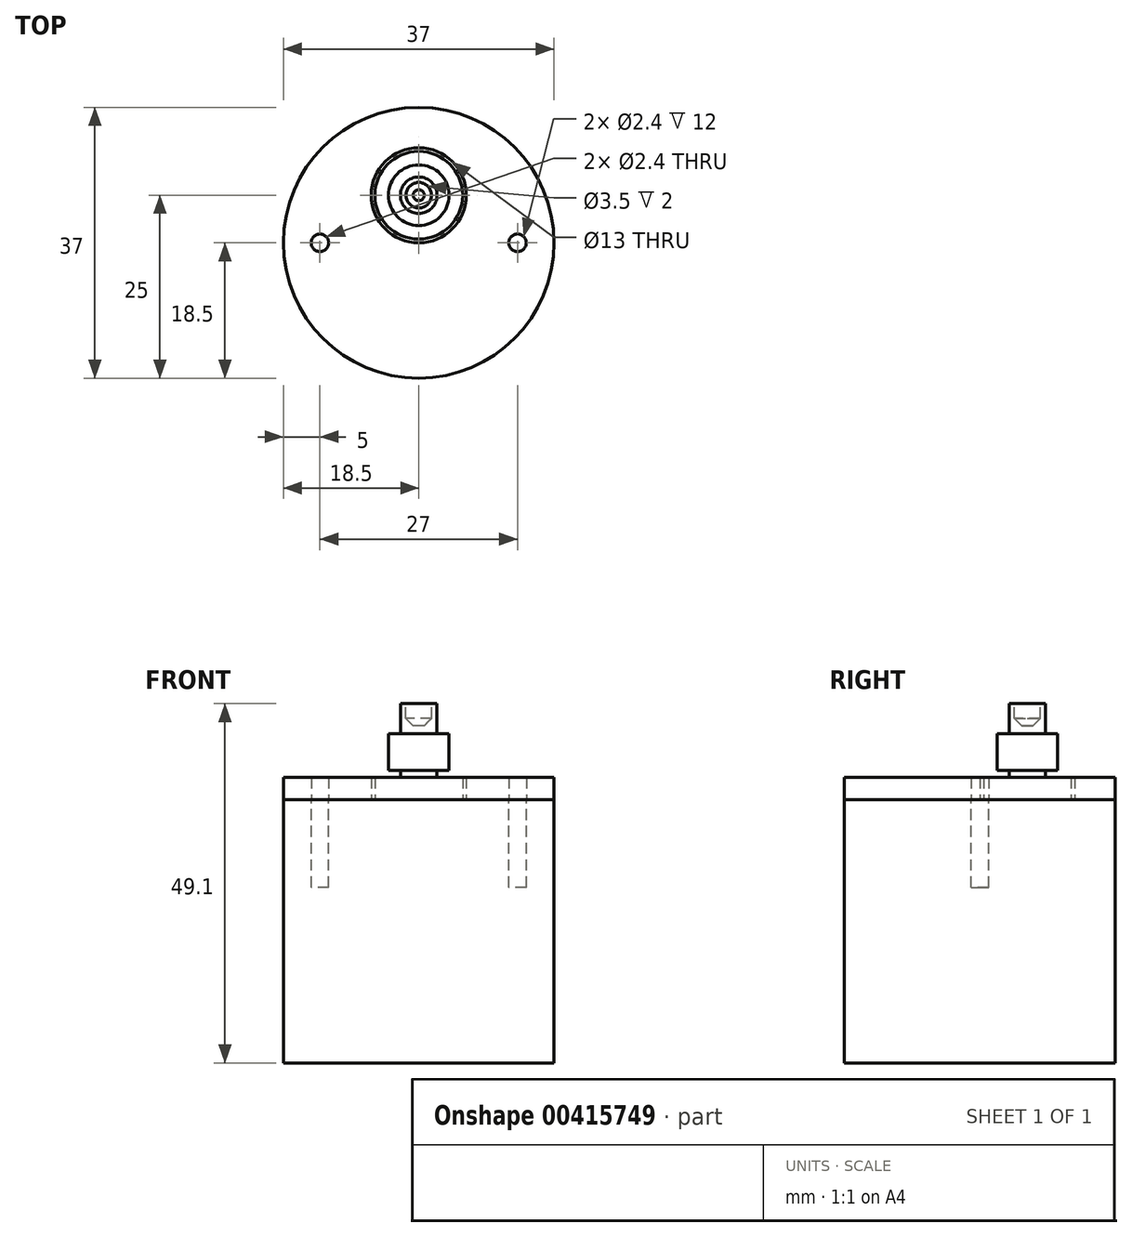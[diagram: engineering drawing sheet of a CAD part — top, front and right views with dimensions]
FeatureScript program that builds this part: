
annotation { "Feature Type Name" : "Feature", "Feature Type Description" : "" }
export const myFeature = defineFeature(function(context is Context, id is Id, definition is map)
    precondition{}
    {
        {
            var Q0;
            Q0=qCreatedBy(makeId("Top.planeOp"),FACE);
            var sketch = newSketch(context, id + "F0", { "sketchPlane" : qUnion([Q0])});
            skCircle(sketch, "E0", {"center": v(0, 0) * mm, "radius": 18.5 * mm});
            skSolve(sketch);
        }
        {
            var Q0;
            Q0=makeQuery(id+"F0.imprint","IMPRINT",FACE,{"disambiguationData":[TD([[makeQuery(id+"F0.imprint","IMPRINT",EDGE,{"derivedFrom":sQuery(id+"F0.wireOp",EDGE,"E0")}),1.0]])]});
            var Q1;
            Q1=sQuery(id+"F0.wireOp",EDGE,"E0");
            extrude(context, id + "F1", {"entities" : qUnion([Q0]), "surfaceEntities" : qUnion([Q1]), "oppositeDirection" : true, "depth" : 36 * mm});
        }
        {
            var Q0;
            Q0=makeQuery(id+"F1.opExtrude","CAP_FACE",FACE,{"disambiguationData":[OSD([sQuery(id+"F0.wireOp",EDGE,"E0")])],"isStart":true});
            var sketch = newSketch(context, id + "F2", { "sketchPlane" : qUnion([Q0])});
            skCircle(sketch, "E1", {"center": v(0, 6.5) * mm, "radius": 6 * mm});
            skCircle(sketch, "E2", {"center": v(-13.5, 0) * mm, "radius": 1.2 * mm});
            skCircle(sketch, "E3", {"center": v(13.5, 0) * mm, "radius": 1.2 * mm});
            skSolve(sketch);
        }
        {
            var Q0;
            Q0=makeQuery(id+"F2.imprint","IMPRINT",FACE,{"disambiguationData":[TD([[makeQuery(id+"F2.imprint","IMPRINT",EDGE,{"derivedFrom":sQuery(id+"F2.wireOp",EDGE,"E2")}),1.0]])]});
            var Q1;
            Q1=makeQuery(id+"F2.imprint","IMPRINT",FACE,{"disambiguationData":[TD([[makeQuery(id+"F2.imprint","IMPRINT",EDGE,{"derivedFrom":sQuery(id+"F2.wireOp",EDGE,"E3")}),1.0]])]});
            var Q2;
            Q2=sQuery(id+"F2.wireOp",EDGE,"E2");
            var Q3;
            Q3=sQuery(id+"F2.wireOp",EDGE,"E3");
            extrude(context, id + "F3", {"entities" : qUnion([Q0, Q1]), "operationType" : NewBodyOperationType.REMOVE, "surfaceEntities" : qUnion([Q2, Q3]), "oppositeDirection" : true, "depth" : 12 * mm});
        }
        {
            var Q0;
            Q0=makeQuery(id+"F2.imprint","IMPRINT",FACE,{"disambiguationData":[TD([[makeQuery(id+"F2.imprint","IMPRINT",EDGE,{"derivedFrom":sQuery(id+"F2.wireOp",EDGE,"E1")}),1.0]])]});
            extrude(context, id + "F4", {"entities" : qUnion([Q0]), "operationType" : NewBodyOperationType.ADD, "depth" : 3 * mm});
        }
        {
            var Q0;
            Q0=makeQuery(id+"F4.opExtrude","CAP_FACE",FACE,{"disambiguationData":[OSD([sQuery(id+"F2.wireOp",EDGE,"E1")])],"isStart":false});
            var sketch = newSketch(context, id + "F5", { "sketchPlane" : qUnion([Q0])});
            skCircle(sketch, "E4", {"center": v(0, 6.5) * mm, "radius": 2.5 * mm});
            skSolve(sketch);
        }
        {
            var Q0;
            Q0=makeQuery(id+"F5.imprint","IMPRINT",FACE,{"disambiguationData":[TD([[makeQuery(id+"F5.imprint","IMPRINT",EDGE,{"derivedFrom":sQuery(id+"F5.wireOp",EDGE,"E4")}),1.0]])]});
            extrude(context, id + "F6", {"entities" : qUnion([Q0]), "operationType" : NewBodyOperationType.ADD, "depth" : 1 * mm});
        }
        {
            var Q0;
            Q0=makeQuery(id+"F6.opExtrude","CAP_FACE",FACE,{"disambiguationData":[OSD([sQuery(id+"F5.wireOp",EDGE,"E4")])],"isStart":false});
            var sketch = newSketch(context, id + "F7", { "sketchPlane" : qUnion([Q0])});
            skCircle(sketch, "E5", {"center": v(0, 6.5) * mm, "radius": 4.15 * mm});
            skSolve(sketch);
        }
        {
            var Q0;
            Q0=makeQuery(id+"F7.imprint","IMPRINT",FACE,{"disambiguationData":[TD([[makeQuery(id+"F7.imprint","IMPRINT",EDGE,{"derivedFrom":sQuery(id+"F7.wireOp",EDGE,"E5")}),1.0]])]});
            var Q1;
            Q1=makeQuery(id+"F7.imprint","IMPRINT",FACE,{"disambiguationData":[TD([[makeQuery(id+"F7.imprint","IMPRINT",EDGE,{"derivedFrom":makeQuery(id+"F6.opExtrude","CAP_EDGE",EDGE,{"disambiguationData":[OSD([sQuery(id+"F5.wireOp",EDGE,"E4")])],"isStart":false})}),1.0]])]});
            extrude(context, id + "F8", {"entities" : qUnion([Q0, Q1]), "operationType" : NewBodyOperationType.ADD, "depth" : 5 * mm});
        }
        {
            var Q0;
            Q0=makeQuery(id+"F8.opExtrude","CAP_FACE",FACE,{"disambiguationData":[OSD([sQuery(id+"F7.wireOp",EDGE,"E5")])],"isStart":false});
            var sketch = newSketch(context, id + "F9", { "sketchPlane" : qUnion([Q0])});
            skCircle(sketch, "E6", {"center": v(0, 6.5) * mm, "radius": 2.5 * mm});
            skSolve(sketch);
        }
        {
            var Q0;
            Q0=makeQuery(id+"F9.imprint","IMPRINT",FACE,{"disambiguationData":[TD([[makeQuery(id+"F9.imprint","IMPRINT",EDGE,{"derivedFrom":sQuery(id+"F9.wireOp",EDGE,"E6")}),1.0]])]});
            var Q1;
            Q1=sQuery(id+"F9.wireOp",EDGE,"E6");
            extrude(context, id + "F10", {"entities" : qUnion([Q0]), "operationType" : NewBodyOperationType.ADD, "surfaceEntities" : qUnion([Q1]), "depth" : 4.1 * mm});
        }
        {
            var Q0;
            Q0=makeQuery(id+"F10.opExtrude","CAP_FACE",FACE,{"disambiguationData":[OSD([sQuery(id+"F9.wireOp",EDGE,"E6")])],"isStart":false});
            var sketch = newSketch(context, id + "F11", { "sketchPlane" : qUnion([Q0])});
            skCircle(sketch, "E7", {"center": v(0, 6.5) * mm, "radius": 1.75 * mm});
            skSolve(sketch);
        }
        {
            var Q0;
            Q0=makeQuery(id+"F11.imprint","IMPRINT",FACE,{"disambiguationData":[TD([[makeQuery(id+"F11.imprint","IMPRINT",EDGE,{"derivedFrom":sQuery(id+"F11.wireOp",EDGE,"E7")}),1.0]])]});
            extrude(context, id + "F12", {"entities" : qUnion([Q0]), "operationType" : NewBodyOperationType.REMOVE, "oppositeDirection" : true, "depth" : 3 * mm});
        }
        {
            var Q0;
            Q0=makeQuery(id+"F12.boolean.opBoolean","COPY",FACE,{"derivedFrom":makeQuery(id+"F12.opExtrude","CAP_FACE",FACE,{"disambiguationData":[OSD([sQuery(id+"F11.wireOp",EDGE,"E7")])],"isStart":false})});
            chamfer(context, id + "F13", {"entities" : qUnion([Q0]), "width" : 1 * mm, "tangentPropagation" : true});
        }
        {
            var Q0;
            Q0=makeQuery(id+"F1.opExtrude","CAP_FACE",FACE,{"disambiguationData":[OSD([sQuery(id+"F0.wireOp",EDGE,"E0")])],"isStart":true});
            var sketch = newSketch(context, id + "F14", { "sketchPlane" : qUnion([Q0])});
            skCircle(sketch, "E8", {"center": v(0, 0) * mm, "radius": 18.5 * mm});
            skCircle(sketch, "E9.0", {"center": v(-13.5, 0) * mm, "radius": 1.2 * mm});
            skCircle(sketch, "E9.1", {"center": v(13.5, 0) * mm, "radius": 1.2 * mm});
            skCircle(sketch, "E10", {"center": v(0, 6.5) * mm, "radius": 6.5 * mm});
            skSolve(sketch);
        }
        {
            var Q0;
            Q0=makeQuery(id+"F14.imprint","IMPRINT",FACE,{"disambiguationData":[TD([[makeQuery(id+"F14.imprint","IMPRINT",EDGE,{"derivedFrom":sQuery(id+"F14.wireOp",EDGE,"E8")}),1.0]])]});
            var Q1;
            Q1=makeQuery(id+"F4.opExtrude","CAP_FACE",FACE,{"disambiguationData":[OSD([sQuery(id+"F2.wireOp",EDGE,"E1")])],"isStart":false});
            extrude(context, id + "F15", {"entities" : qUnion([Q0]), "endBound" : BoundingType.UP_TO_SURFACE, "endBoundEntityFace" : qUnion([Q1]), "depth" : 25 * mm});
        }
        {
            var Q0;
            Q0=makeQuery(id+"F15.opExtrude","CAP_FACE",FACE,{"disambiguationData":[OSD([sQuery(id+"F14.wireOp",EDGE,"E8"),sQuery(id+"F14.wireOp",EDGE,"E9.0"),sQuery(id+"F14.wireOp",EDGE,"E9.1"),sQuery(id+"F14.wireOp",EDGE,"E10")])],"isStart":false});
            cPlane(context, id + "F16", {"entities" : qUnion([Q0]), "cplaneType" : CPlaneType.OFFSET, "offset" : 0.5 * mm, "width" : 150 * mm, "height" : 150 * mm});
        }
    });
